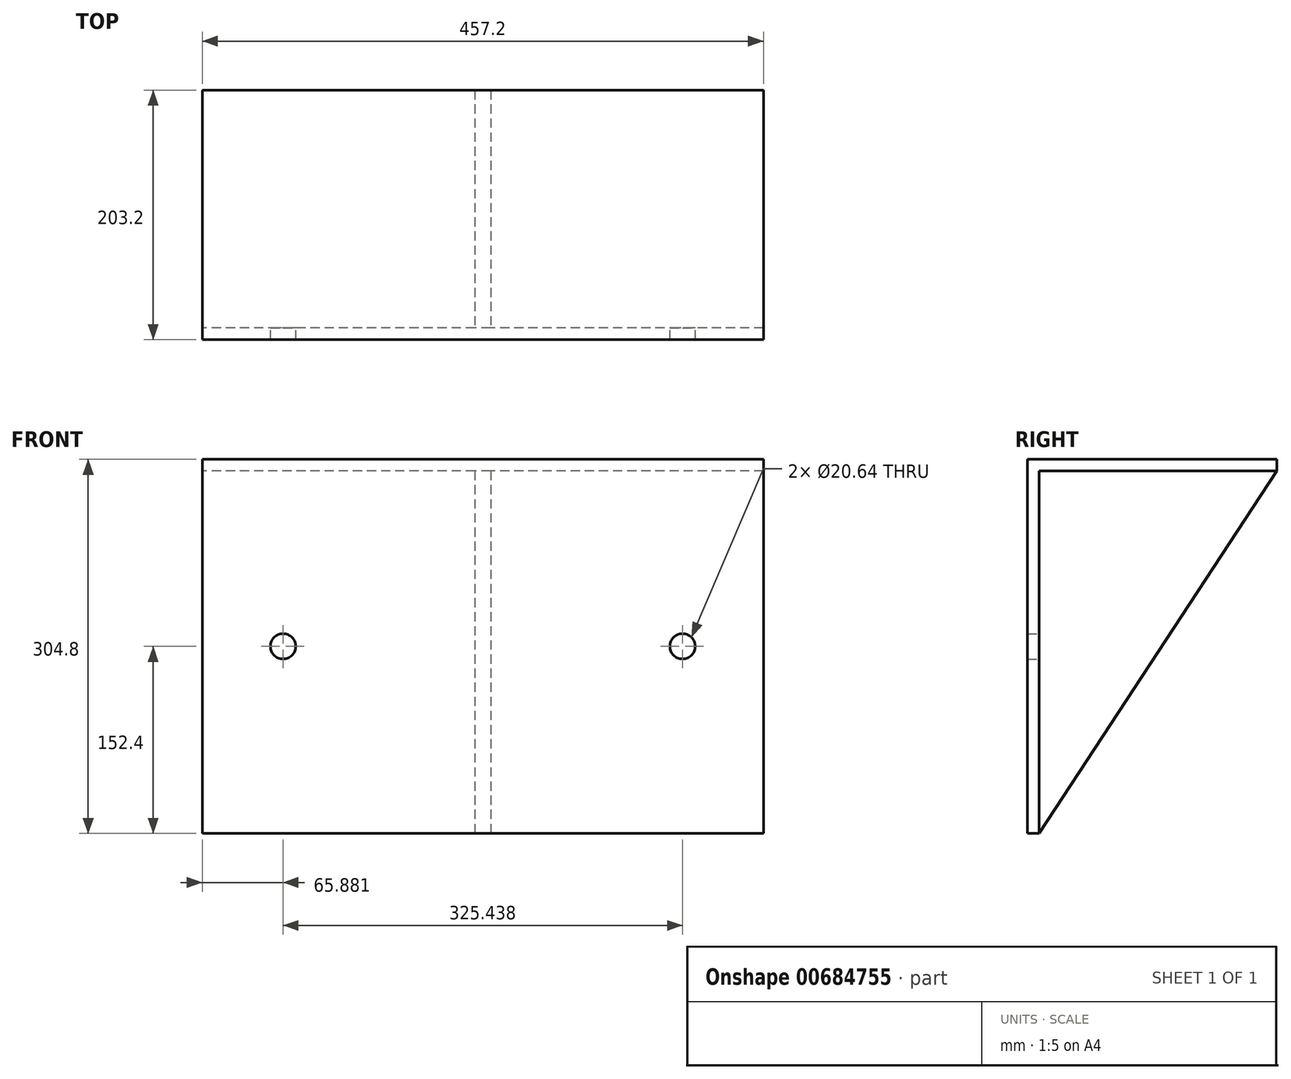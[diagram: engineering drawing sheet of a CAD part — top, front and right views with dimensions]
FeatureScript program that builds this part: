
annotation { "Feature Type Name" : "Feature", "Feature Type Description" : "" }
export const myFeature = defineFeature(function(context is Context, id is Id, definition is map)
    precondition{}
    {
        {
            var Q0;
            Q0=qCreatedBy(makeId("Right.planeOp"),FACE);
            var sketch = newSketch(context, id + "F0", { "sketchPlane" : qUnion([Q0])});
            skLineSegment(sketch, "E0", {"start": v(101.6, 152.4) * mm, "end": v(-101.6, 152.4) * mm});
            skLineSegment(sketch, "E1", {"start": v(-101.6, 152.4) * mm, "end": v(-101.6, -152.4) * mm});
            skLineSegment(sketch, "E2", {"start": v(-101.6, -152.4) * mm, "end": v(-92.07, -152.4) * mm});
            skLineSegment(sketch, "E3", {"start": v(-92.07, -152.4) * mm, "end": v(-92.08, 142.88) * mm});
            skLineSegment(sketch, "E4", {"start": v(-92.08, 142.87) * mm, "end": v(101.6, 142.87) * mm});
            skLineSegment(sketch, "E5", {"start": v(101.6, 142.88) * mm, "end": v(101.6, 152.4) * mm});
            skPoint(sketch, "E6", {"position": v(0, 152.4) * mm});
            skPoint(sketch, "E7", {"position": v(-101.6, 0) * mm});
            skSolve(sketch);
        }
        {
            var Q0;
            Q0=qSketchRegion(id+"F0",true);
            extrude(context, id + "F1", {"entities" : qUnion([Q0]), "endBound" : BoundingType.SYMMETRIC, "depth" : 457.2 * mm, "offsetDistance" : 25.4 * mm});
        }
        {
            var Q0;
            Q0=qCreatedBy(makeId("Right.planeOp"),FACE);
            var sketch = newSketch(context, id + "F2", { "sketchPlane" : qUnion([Q0])});
            skLineSegment(sketch, "E8", {"start": v(101.6, 142.88) * mm, "end": v(-92.08, 142.87) * mm});
            skLineSegment(sketch, "E9", {"start": v(-92.08, 142.87) * mm, "end": v(-92.08, -152.4) * mm});
            skLineSegment(sketch, "E10", {"start": v(-92.07, -152.4) * mm, "end": v(101.6, 142.88) * mm});
            skSolve(sketch);
        }
        {
            var Q0;
            Q0=qSketchRegion(id+"F2",true);
            extrude(context, id + "F3", {"entities" : qUnion([Q0]), "operationType" : NewBodyOperationType.ADD, "endBound" : BoundingType.SYMMETRIC, "depth" : 12.7 * mm, "offsetDistance" : 25.4 * mm});
        }
        {
            var Q0;
            {var subQ0=sQuery(id+"F2.wireOp",EDGE,"E10");var subQ3=sQuery(id+"F0.wireOp",EDGE,"E3");Q0=makeQuery(id+"F3.boolean.opBoolean","SPLIT",FACE,{"disambiguationData":[TD([makeQuery(id+"F3.opExtrude","CAP_FACE",FACE,{"disambiguationData":[OSD([sQuery(id+"F2.wireOp",EDGE,"E8"),sQuery(id+"F2.wireOp",EDGE,"E9"),subQ0])],"isStart":false})])],"derivedFrom":makeQuery(id+"F1.opExtrude","SWEPT_FACE",FACE,{"disambiguationData":[OSD([subQ3])]})});}
            var sketch = newSketch(context, id + "F4", { "sketchPlane" : qUnion([Q0])});
            skCircle(sketch, "E11", {"center": v(-162.72, 0) * mm, "radius": 10.32 * mm});
            skCircle(sketch, "E12", {"center": v(162.72, 0) * mm, "radius": 10.32 * mm});
            skLineSegment(sketch, "E13", {"start": v(-162.72, 0) * mm, "end": v(162.72, 0) * mm, "construction": true});
            skSolve(sketch);
        }
        {
            var Q0;
            Q0=qSketchRegion(id+"F4",true);
            extrude(context, id + "F5", {"entities" : qUnion([Q0]), "operationType" : NewBodyOperationType.REMOVE, "oppositeDirection" : true, "depth" : 25.4 * mm, "offsetDistance" : 25.4 * mm});
        }
    });
